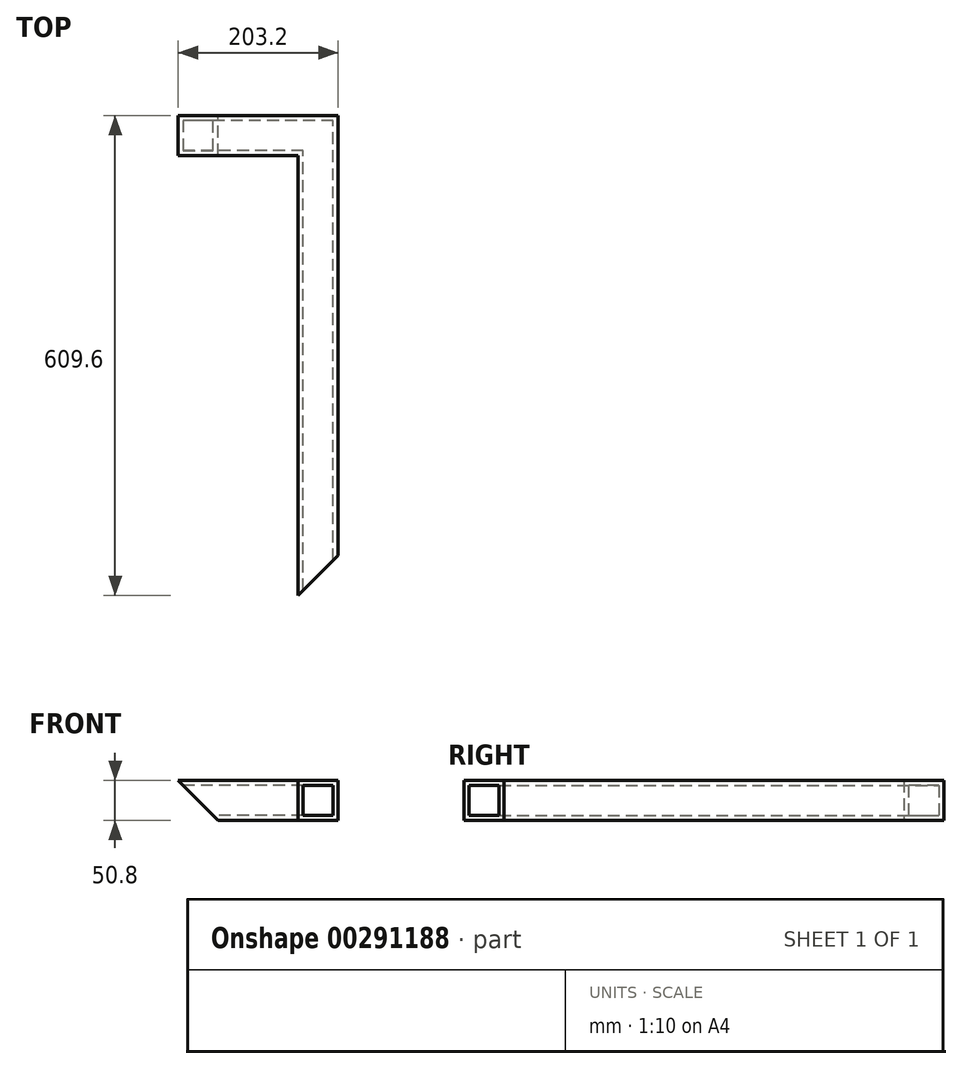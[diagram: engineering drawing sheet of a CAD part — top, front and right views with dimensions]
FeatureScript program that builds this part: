
annotation { "Feature Type Name" : "Feature", "Feature Type Description" : "" }
export const myFeature = defineFeature(function(context is Context, id is Id, definition is map)
    precondition{}
    {
        {
            var Q0;
            Q0=qCreatedBy(makeId("Top.planeOp"),FACE);
            var sketch = newSketch(context, id + "F0", { "sketchPlane" : qUnion([Q0])});
            skLineSegment(sketch, "E0", {"start": v(0, 0) * mm, "end": v(0, 584.2) * mm});
            skLineSegment(sketch, "E1", {"start": v(0, 584.2) * mm, "end": v(-177.8, 584.2) * mm});
            skSolve(sketch);
        }
        {
            var Q0;
            Q0=qCreatedBy(makeId("Front.planeOp"),FACE);
            var sketch = newSketch(context, id + "F1", { "sketchPlane" : qUnion([Q0])});
            skLineSegment(sketch, "E2.bottom", {"start": v(25.4, -25.4) * mm, "end": v(-25.4, -25.4) * mm});
            skLineSegment(sketch, "E2.top", {"start": v(25.4, 25.4) * mm, "end": v(-25.4, 25.4) * mm});
            skLineSegment(sketch, "E2.left", {"start": v(25.4, -25.4) * mm, "end": v(25.4, 25.4) * mm});
            skLineSegment(sketch, "E2.right", {"start": v(-25.4, -25.4) * mm, "end": v(-25.4, 25.4) * mm});
            skPoint(sketch, "E2.middle", {"position": v(0, 0) * mm});
            skLineSegment(sketch, "E3.0", {"start": v(19.05, 19.05) * mm, "end": v(-19.05, 19.05) * mm});
            skLineSegment(sketch, "E3.1", {"start": v(19.05, -19.05) * mm, "end": v(19.05, 19.05) * mm});
            skLineSegment(sketch, "E3.2", {"start": v(19.05, -19.05) * mm, "end": v(-19.05, -19.05) * mm});
            skLineSegment(sketch, "E3.3", {"start": v(-19.05, -19.05) * mm, "end": v(-19.05, 19.05) * mm});
            skSolve(sketch);
        }
        {
            var Q0;
            Q0=qSketchRegion(id+"F1",true);
            var Q1;
            Q1=qConstructionFilter(qBodyType(qCreatedBy(id+"F0",EDGE),BodyType.WIRE),ConstructionObject.NO);
            sweep(context, id + "F2", {"profiles" : qUnion([Q0]), "path" : qUnion([Q1])});
        }
        {
            var Q0;
            Q0=makeQuery(id+"F2.opSweep","SWEPT_FACE",FACE,{"disambiguationData":[OSD([sQuery(id+"F0.wireOp",EDGE,"E0"),sQuery(id+"F1.wireOp",EDGE,"E2.top")])]});
            var sketch = newSketch(context, id + "F3", { "sketchPlane" : qUnion([Q0])});
            skLineSegment(sketch, "E4", {"start": v(25.4, 0) * mm, "end": v(-25.4, 0) * mm});
            skLineSegment(sketch, "E5", {"start": v(-25.4, 0) * mm, "end": v(25.4, 50.8) * mm});
            skLineSegment(sketch, "E6", {"start": v(25.4, 50.8) * mm, "end": v(25.4, 0) * mm});
            skSolve(sketch);
        }
        {
            var Q0;
            Q0 = qSketchRegion(id + "F3", true);
            extrude(context, id + "F4", {"entities" : qUnion([Q0]), "operationType" : NewBodyOperationType.REMOVE, "endBound" : BoundingType.THROUGH_ALL, "oppositeDirection" : true, "depth" : 25.4 * mm});
        }
        {
            var Q0;
            Q0=makeQuery(id+"F2.opSweep","SWEPT_FACE",FACE,{"disambiguationData":[OSD([sQuery(id+"F0.wireOp",EDGE,"E1"),sQuery(id+"F1.wireOp",EDGE,"E2.left")])]});
            var sketch = newSketch(context, id + "F5", { "sketchPlane" : qUnion([Q0])});
            skLineSegment(sketch, "E7", {"start": v(177.8, 25.4) * mm, "end": v(127, -25.4) * mm});
            skLineSegment(sketch, "E8", {"start": v(127, -25.4) * mm, "end": v(177.8, -25.4) * mm});
            skLineSegment(sketch, "E9", {"start": v(177.8, -25.4) * mm, "end": v(177.8, 25.4) * mm});
            skSolve(sketch);
        }
        {
            var Q0;
            Q0 = qSketchRegion(id + "F5", true);
            extrude(context, id + "F6", {"entities" : qUnion([Q0]), "operationType" : NewBodyOperationType.REMOVE, "endBound" : BoundingType.THROUGH_ALL, "oppositeDirection" : true, "depth" : 25.4 * mm});
        }
    });
